MODEL slx_d5284c8b97ff
KIND model
CONFIG AbsTol = auto
CONFIG EnableMultiTasking = off
CONFIG FixedStep = auto
CONFIG MaxStep = auto
CONFIG MinStep = auto
CONFIG RelTol = 1e-3
CONFIG SampleTimeConstraint = Unconstrained
CONFIG SolverName = ode45
CONFIG StartTime = 0.0
CONFIG StopTime = 20
BLOCK [TransferFcn] Lag controller 
  Denominator = [Tr 1]
BLOCK [TransferFcn] Lag controller 2
  Denominator = [Ta 1]
  Numerator = [K]
BLOCK [TransferFcn] Lead-Lag controller 
  Denominator = [Tb 1]
  Numerator = [Tc 1]
BLOCK [Scope] Scope
  Floating = off
  NumInputPorts = 1
  ScopeSpecificationString = Simulink.scopes.TimeScopeBlockCfg('CurrentConfiguration', extmgr.ConfigurationSet(extmgr.Configuration('Core','General UI',true),extmgr.Configuration('Core','Source UI',true),extmgr.Configuration('Sources','WiredSimulink',true),extmgr.Configuration('Visuals','Time Domain',true,'SerializedDisplays',{struct('MinYLimReal','-0.1125','MaxYLimReal','0.0125','YLabelReal','','MinYLimMag','0.00000','MaxYLi...<+1347ch>
BLOCK [Step] Step
  SampleTime = 0
  Time = 0
BLOCK [Step] Step1
  SampleTime = 0
  Time = 100
BLOCK [Sum] Sum
  IconShape = rectangular
  Inputs = +|--
BLOCK [ToWorkspace] To Workspace
  FixptAsFi = on
  MaxDataPoints = inf
  SampleTime = -1
  SaveFormat = Timeseries
  VariableName = Efd
BLOCK [ToWorkspace] To Workspace1
  FixptAsFi = on
  MaxDataPoints = inf
  SampleTime = -1
  SaveFormat = Timeseries
  VariableName = Vref
BLOCK [ToWorkspace] To Workspace2
  FixptAsFi = on
  MaxDataPoints = inf
  SampleTime = -1
  SaveFormat = Timeseries
  VariableName = VT
BLOCK [TransferFcn] Transfer Fcn3
  Denominator = [Tf 1]
  Numerator = [Kf 0]
ANNOTATION (root): Transient gain reduction
ANNOTATION (root): Prof F. Gonzalez-Longatt <email> https://github.com/fglongatt
ANNOTATION (root): NOTE: This model requires the script: SS_Exciter_Rogers_Comparison.slx
ANNOTATION (root): Example shown in Chapter [1] G. Rogers, Power system oscillations . London: Kluwer Academic , 2000.
ANNOTATION (root): Space-State Representation: Simple excitation system
ANNOTATION (root): Exciter power amplifier
ANNOTATION (root): Transient output feedback
ANNOTATION (root): Voltage transducer
NET Lag controller 2:1 -> Scope:1, To Workspace:1, Transfer Fcn3:1
LINE Lag controller :1 -> Sum:2
LINE Lead-Lag controller :1 -> Lag controller 2:1
NET Step1:1 -> Sum:1, To Workspace1:1
NET Step:1 -> Lag controller :1, To Workspace2:1
LINE Sum:1 -> Lead-Lag controller :1
LINE Transfer Fcn3:1 -> Sum:3
note: NET lines group one-source signal fan-out (src -> all destinations, sorted); 1:1 wires keep LINE
